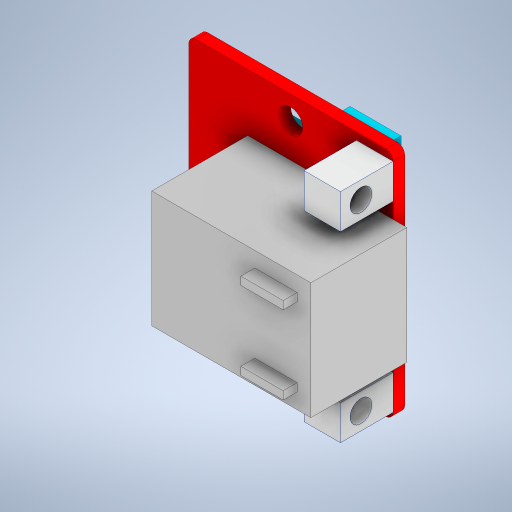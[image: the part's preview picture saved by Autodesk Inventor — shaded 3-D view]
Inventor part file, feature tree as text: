
AUTODESK INVENTOR PART (.ipt)
format: ipt  version: 2024 (Build 280153000, 153)  size: 367,616 bytes
history: native  units: mm
features: extrude x7, sketch x7, projected_geometry x2, fillet x1
ambient origin geometry x8: Origin, YZ Plane, XZ Plane, XY Plane, X Axis, Y Axis, Z Axis, Center Point
bodies: Solid1 (feature_tree), Solid2 (feature_tree), Solid3 (feature_tree), Solid4 (feature_tree), Solid5 (feature_tree)
feature tree (17):
  extrude  "Extrusion1"  Depth=31.75mm
  extrude  "Extrusion2"  Depth=3.26mm
  extrude  "Extrusion3"  Depth=16.0mm
  extrude  "Extrusion4"  Depth=1.89mm
  extrude  "Extrusion5"  Depth=5.8mm
  extrude  "Extrusion6"  Depth=1.1mm
  extrude  "Extrusion7"  Depth=4.75mm
  fillet  "Fillet1"  Radius=25.05mm
  sketch  "Sketch1"  dims[d0=28.0mm d1=31.75mm]
  sketch  "Sketch2"  dims[d2=25.4mm d3=3.26mm]
  sketch  "Sketch3"  dims[d4=1.6mm d5=0.0mm d6=16.0mm]
  projected_geometry  "Projected Loop1"
  sketch  "Sketch4"  dims[d7=21.8mm d8=1.89mm]
  projected_geometry  "Projected Loop2"
  sketch  "Sketch5"  dims[d9=13.15mm d10=0.0mm d11=5.8mm]
  sketch  "Sketch6"  dims[d12=3.2mm d13=1.1mm]
  sketch  "Sketch7"  dims[d14=1.9mm d15=0.0mm d16=4.75mm d18=25.05mm d19=7.2mm d20=0.0mm d21=3.0mm d22=4.4mm d23=7.2mm d24=0.0mm d25=15.3mm d26=3.0mm d27=3.3mm d28=2.0mm d29=0.0mm d30=1.0mm d31=2.5mm d32=2.5mm d33=5.0mm d34=7.0mm d35=18.0mm d36=2.0mm d37=0.0mm d38=1.0mm]
